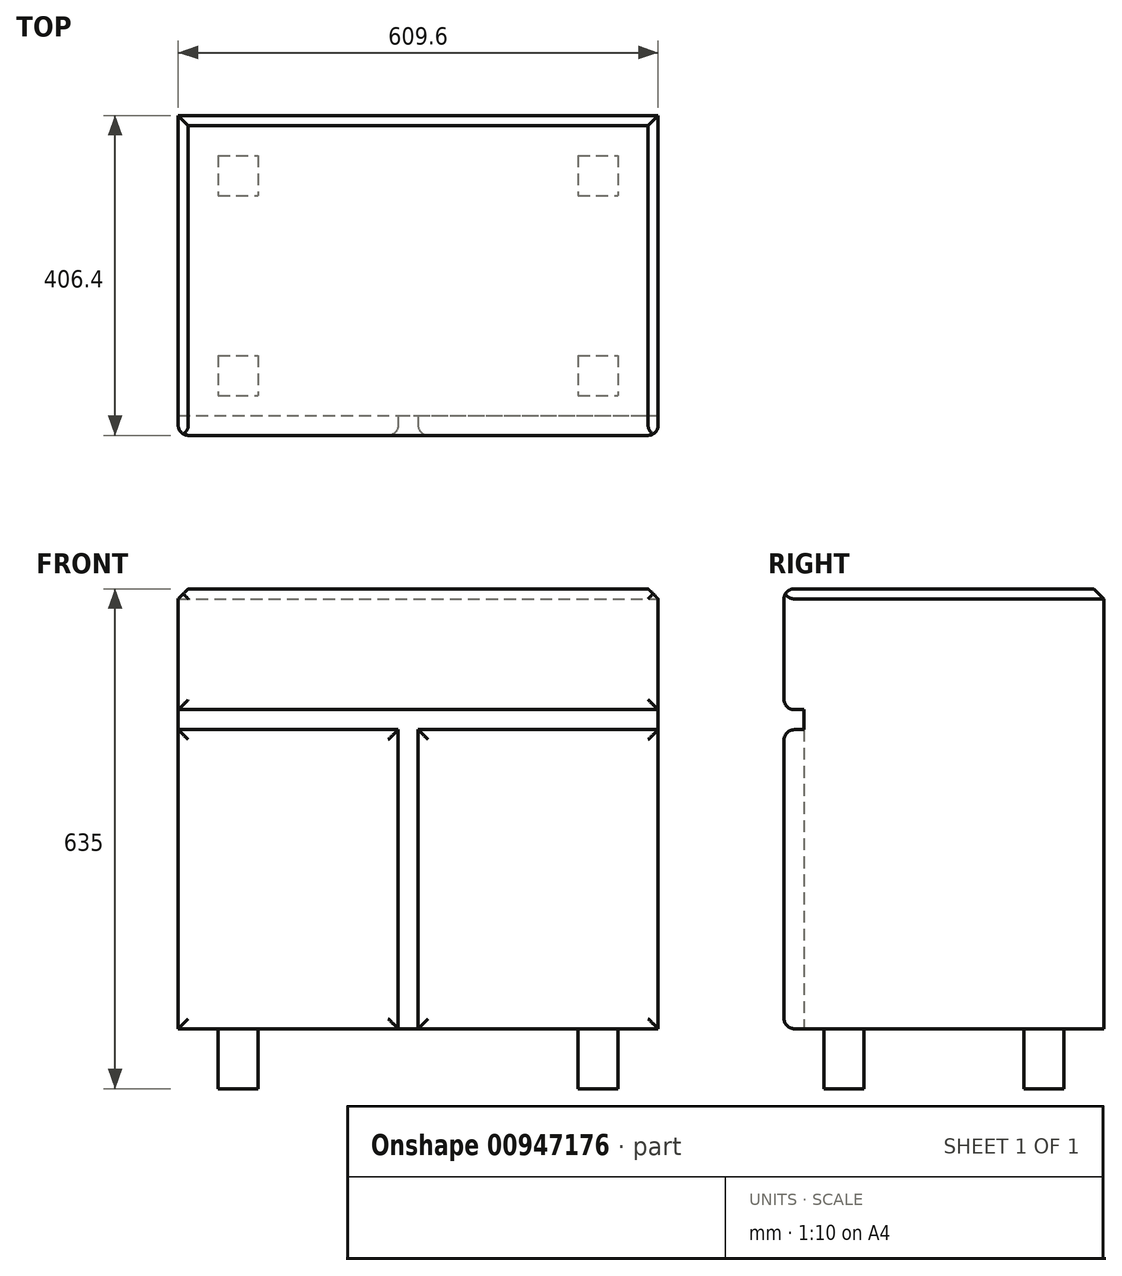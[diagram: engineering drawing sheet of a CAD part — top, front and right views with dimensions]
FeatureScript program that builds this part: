
annotation { "Feature Type Name" : "Feature", "Feature Type Description" : "" }
export const myFeature = defineFeature(function(context is Context, id is Id, definition is map)
    precondition{}
    {
        {
            var Q0;
            Q0=qCreatedBy(makeId("Top.planeOp"),FACE);
            var sketch = newSketch(context, id + "F0", { "sketchPlane" : qUnion([Q0])});
            skLineSegment(sketch, "E0.bottom", {"start": v(0, 0) * mm, "end": v(609.6, 0) * mm});
            skLineSegment(sketch, "E0.top", {"start": v(0, 381) * mm, "end": v(609.6, 381) * mm});
            skLineSegment(sketch, "E0.left", {"start": v(0, 0) * mm, "end": v(0, 381) * mm});
            skLineSegment(sketch, "E0.right", {"start": v(609.6, 0) * mm, "end": v(609.6, 381) * mm});
            skSolve(sketch);
        }
        {
            var Q0;
            Q0 = qSketchRegion(id + "F0", true);
            extrude(context, id + "F1", {"entities" : qUnion([Q0]), "depth" : 635 * mm, "offsetDistance" : 25.4 * mm});
        }
        {
            var Q0;
            Q0=makeQuery(id+"F1.opExtrude","SWEPT_FACE",FACE,{"disambiguationData":[OSD([sQuery(id+"F0.wireOp",EDGE,"E0.bottom")])]});
            extrude(context, id + "F2", {"entities" : qUnion([Q0]), "operationType" : NewBodyOperationType.ADD, "depth" : 25.4 * mm, "offsetDistance" : 25.4 * mm});
        }
        {
            var Q0;
            Q0=makeQuery(id+"F2.opExtrude","CAP_FACE",FACE,{"disambiguationData":[OSD([sQuery(id+"F0.wireOp",EDGE,"E0.bottom")])],"isStart":false});
            var sketch = newSketch(context, id + "F3", { "sketchPlane" : qUnion([Q0])});
            skLineSegment(sketch, "E1.bottom", {"start": v(0, 76.2) * mm, "end": v(50.8, 76.2) * mm});
            skLineSegment(sketch, "E1.top", {"start": v(0, 0) * mm, "end": v(50.8, 0) * mm});
            skLineSegment(sketch, "E1.left", {"start": v(0, 76.2) * mm, "end": v(0, 0) * mm});
            skLineSegment(sketch, "E1.right", {"start": v(50.8, 76.2) * mm, "end": v(50.8, 0) * mm});
            skLineSegment(sketch, "E2.bottom", {"start": v(101.6, 76.2) * mm, "end": v(508, 76.2) * mm});
            skLineSegment(sketch, "E2.top", {"start": v(101.6, 0) * mm, "end": v(508, 0) * mm});
            skLineSegment(sketch, "E2.left", {"start": v(101.6, 76.2) * mm, "end": v(101.6, 0) * mm});
            skLineSegment(sketch, "E2.right", {"start": v(508, 76.2) * mm, "end": v(508, 0) * mm});
            skLineSegment(sketch, "E3.bottom", {"start": v(558.8, 76.2) * mm, "end": v(609.6, 76.2) * mm});
            skLineSegment(sketch, "E3.top", {"start": v(558.8, 0) * mm, "end": v(609.6, 0) * mm});
            skLineSegment(sketch, "E3.left", {"start": v(558.8, 76.2) * mm, "end": v(558.8, 0) * mm});
            skLineSegment(sketch, "E3.right", {"start": v(609.6, 76.2) * mm, "end": v(609.6, 0) * mm});
            skSolve(sketch);
        }
        {
            var Q0;
            Q0 = qSketchRegion(id + "F3", true);
            extrude(context, id + "F4", {"entities" : qUnion([Q0]), "operationType" : NewBodyOperationType.REMOVE, "oppositeDirection" : true, "depth" : 1574.8 * mm, "offsetDistance" : 25.4 * mm});
        }
        {
            var Q0;
            Q0=makeQuery(id+"F4.boolean.opBoolean","COPY",FACE,{"derivedFrom":makeQuery(id+"F4.opExtrude","SWEPT_FACE",FACE,{"disambiguationData":[OSD([sQuery(id+"F3.wireOp",EDGE,"E3.left")])]})});
            var sketch = newSketch(context, id + "F5", { "sketchPlane" : qUnion([Q0])});
            skLineSegment(sketch, "E4.bottom", {"start": v(-25.4, 76.2) * mm, "end": v(25.4, 76.2) * mm});
            skLineSegment(sketch, "E4.top", {"start": v(-25.4, 0) * mm, "end": v(25.4, 0) * mm});
            skLineSegment(sketch, "E4.left", {"start": v(-25.4, 76.2) * mm, "end": v(-25.4, 0) * mm});
            skLineSegment(sketch, "E4.right", {"start": v(25.4, 76.2) * mm, "end": v(25.4, 0) * mm});
            skLineSegment(sketch, "E5.bottom", {"start": v(76.2, 76.2) * mm, "end": v(279.4, 76.2) * mm});
            skLineSegment(sketch, "E5.top", {"start": v(76.2, 0) * mm, "end": v(279.4, 0) * mm});
            skLineSegment(sketch, "E5.left", {"start": v(76.2, 76.2) * mm, "end": v(76.2, 0) * mm});
            skLineSegment(sketch, "E5.right", {"start": v(279.4, 76.2) * mm, "end": v(279.4, 0) * mm});
            skLineSegment(sketch, "E6.bottom", {"start": v(381, 76.2) * mm, "end": v(330.2, 76.2) * mm});
            skLineSegment(sketch, "E6.top", {"start": v(381, 0) * mm, "end": v(330.2, 0) * mm});
            skLineSegment(sketch, "E6.left", {"start": v(381, 76.2) * mm, "end": v(381, 0) * mm});
            skLineSegment(sketch, "E6.right", {"start": v(330.2, 76.2) * mm, "end": v(330.2, 0) * mm});
            skSolve(sketch);
        }
        {
            var Q0;
            Q0 = qSketchRegion(id + "F5", true);
            extrude(context, id + "F6", {"entities" : qUnion([Q0]), "operationType" : NewBodyOperationType.REMOVE, "oppositeDirection" : true, "depth" : 970.28 * mm, "offsetDistance" : 25.4 * mm});
        }
        {
            var Q0;
            Q0=makeQuery(id+"F2.opExtrude","CAP_FACE",FACE,{"disambiguationData":[OSD([sQuery(id+"F0.wireOp",EDGE,"E0.bottom")])],"isStart":false});
            var sketch = newSketch(context, id + "F7", { "sketchPlane" : qUnion([Q0])});
            skLineSegment(sketch, "E7.bottom", {"start": v(0, 481.42) * mm, "end": v(609.6, 481.42) * mm});
            skLineSegment(sketch, "E7.top", {"start": v(0, 456.02) * mm, "end": v(609.6, 456.02) * mm});
            skLineSegment(sketch, "E7.left", {"start": v(0, 481.42) * mm, "end": v(0, 456.02) * mm});
            skLineSegment(sketch, "E7.right", {"start": v(609.6, 481.42) * mm, "end": v(609.6, 456.02) * mm});
            skLineSegment(sketch, "E8.bottom", {"start": v(304.8, 456.02) * mm, "end": v(279.4, 456.02) * mm});
            skLineSegment(sketch, "E8.top", {"start": v(304.8, 76.2) * mm, "end": v(279.4, 76.2) * mm});
            skLineSegment(sketch, "E8.left", {"start": v(304.8, 456.02) * mm, "end": v(304.8, 76.2) * mm});
            skLineSegment(sketch, "E8.right", {"start": v(279.4, 456.02) * mm, "end": v(279.4, 76.2) * mm});
            skSolve(sketch);
        }
        {
            var Q0;
            {Q0=qUnion([makeQuery(id+"F7.imprint","IMPRINT",FACE,{"disambiguationData":[TD([[makeQuery(id+"F7.imprint","IMPRINT",EDGE,{"derivedFrom":sQuery(id+"F7.wireOp",EDGE,"E8.top")}),1.0]])]}),makeQuery(id+"F7.imprint","IMPRINT",FACE,{"disambiguationData":[TD([[makeQuery(id+"F7.imprint","IMPRINT",EDGE,{"derivedFrom":sQuery(id+"F7.wireOp",EDGE,"E7.bottom")}),-1.0]])]})]);}
            extrude(context, id + "F8", {"entities" : qUnion([Q0]), "operationType" : NewBodyOperationType.REMOVE, "oppositeDirection" : true, "depth" : 25.4 * mm, "offsetDistance" : 25.4 * mm});
        }
        {
            var Q0;
            {var subQ1=sQuery(id+"F0.wireOp",EDGE,"E0.bottom");Q0=makeQuery(id+"F8.boolean.opBoolean","SPLIT",FACE,{"disambiguationData":[TD([makeQuery(id+"F8.opExtrude","SWEPT_FACE",FACE,{"disambiguationData":[OSD([sQuery(id+"F7.wireOp",EDGE,"E7.bottom")])]})])],"derivedFrom":makeQuery(id+"F2.opExtrude","CAP_FACE",FACE,{"disambiguationData":[OSD([subQ1])],"isStart":false})});}
            var Q1;
            {var subQ1=sQuery(id+"F0.wireOp",EDGE,"E0.bottom");var subQ3=sQuery(id+"F7.wireOp",EDGE,"E8.right");Q1=makeQuery(id+"F8.boolean.opBoolean","SPLIT",FACE,{"disambiguationData":[TD([makeQuery(id+"F8.opExtrude","SWEPT_FACE",FACE,{"disambiguationData":[OSD([subQ3])]})])],"derivedFrom":makeQuery(id+"F2.opExtrude","CAP_FACE",FACE,{"disambiguationData":[OSD([subQ1])],"isStart":false})});}
            var Q2;
            {var subQ1=sQuery(id+"F0.wireOp",EDGE,"E0.bottom");var subQ2=sQuery(id+"F7.wireOp",EDGE,"E8.left");Q2=makeQuery(id+"F8.boolean.opBoolean","SPLIT",FACE,{"disambiguationData":[TD([makeQuery(id+"F8.opExtrude","SWEPT_FACE",FACE,{"disambiguationData":[OSD([subQ2])]})])],"derivedFrom":makeQuery(id+"F2.opExtrude","CAP_FACE",FACE,{"disambiguationData":[OSD([subQ1])],"isStart":false})});}
            fillet(context, id + "F9", {"entities" : qUnion([Q0, Q1, Q2]), "radius" : 12.7 * mm, "tangentPropagation" : true, "allowEdgeOverflow" : false});
        }
        {
            var Q0;
            {var subQ0=sQuery(id+"F0.wireOp",EDGE,"E0.bottom");Q0=makeQuery(id+"F2.boolean.opBoolean","MERGE",FACE,{"derivedFrom":[makeQuery(id+"F1.opExtrude","CAP_FACE",FACE,{"disambiguationData":[OSD([subQ0,sQuery(id+"F0.wireOp",EDGE,"E0.top"),sQuery(id+"F0.wireOp",EDGE,"E0.left"),sQuery(id+"F0.wireOp",EDGE,"E0.right")])],"isStart":false}),makeQuery(id+"F2.opExtrude","SWEPT_FACE",FACE,{"disambiguationData":[OSD([subQ0]),TDD([makeQuery(id+"F1.opExtrude","CAP_EDGE",EDGE,{"disambiguationData":[OSD([subQ0])],"isStart":false})])]})]});}
            chamfer(context, id + "F10", {"entities" : qUnion([Q0]), "width" : 12.7 * mm, "tangentPropagation" : true});
        }
    });
